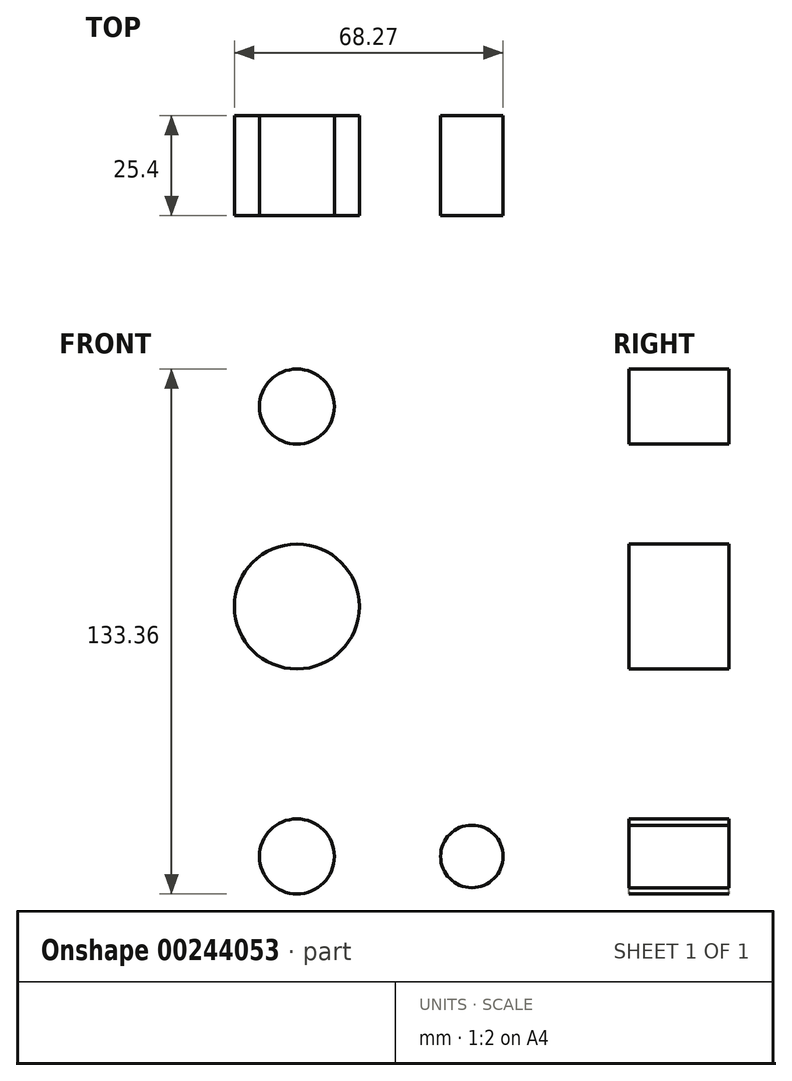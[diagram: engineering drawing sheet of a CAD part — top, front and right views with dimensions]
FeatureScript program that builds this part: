
annotation { "Feature Type Name" : "Feature", "Feature Type Description" : "" }
export const myFeature = defineFeature(function(context is Context, id is Id, definition is map)
    precondition{}
    {
        {
            var Q0;
            Q0=qCreatedBy(makeId("Front.planeOp"),FACE);
            var sketch = newSketch(context, id + "F0", { "sketchPlane" : qUnion([Q0])});
            skCircle(sketch, "E0", {"center": v(0, 0) * mm, "radius": 15.88 * mm});
            skCircle(sketch, "E1", {"center": v(0, 50.8) * mm, "radius": 9.53 * mm});
            skCircle(sketch, "E2", {"center": v(0, -63.5) * mm, "radius": 9.53 * mm});
            skCircle(sketch, "E3", {"center": v(44.45, -63.5) * mm, "radius": 7.94 * mm});
            skSolve(sketch);
        }
        {
            var Q0;
            Q0=qCreatedBy(makeId("Front.planeOp"),FACE);
            var sketch = newSketch(context, id + "F1", { "sketchPlane" : qUnion([Q0])});
            skLineSegment(sketch, "E4", {"start": v(9.46, 51.92) * mm, "end": v(16, 0) * mm});
            skLineSegment(sketch, "E5", {"start": v(16, 0) * mm, "end": v(10.25, -45.67) * mm});
            skLineSegment(sketch, "E6", {"start": v(-9.38, 52.57) * mm, "end": v(-16, 0) * mm});
            skLineSegment(sketch, "E7", {"start": v(-16, 0) * mm, "end": v(-8.14, -62.35) * mm});
            skLineSegment(sketch, "E8", {"start": v(17.85, -54.6) * mm, "end": v(45, -55.58) * mm});
            skLineSegment(sketch, "E9", {"start": v(0, -73.03) * mm, "end": v(45.77, -71.4) * mm});
            skPoint(sketch, "E10.newPointB", {"position": v(0, -53.97) * mm});
            skArc(sketch, "E10.filletArc", {"start": v(10.25, -45.67) * mm, "mid": v(12.08, -51.81) * mm, "end": v(17.85, -54.6) * mm});
            skSolve(sketch);
        }
        {
            var Q0;
            Q0 = qSketchRegion(id + "F0", true);
            var Q1;
            Q1 = qSketchRegion(id + "F1", true);
            extrude(context, id + "F2", {"entities" : qUnion([Q0, Q1]), "depth" : 25.4 * mm});
        }
        {
            var Q0;
            Q0=qCreatedBy(makeId("Front.planeOp"),FACE);
            var sketch = newSketch(context, id + "F3", { "sketchPlane" : qUnion([Q0])});
            skLineSegment(sketch, "E11.bottom", {"start": v(-30.12, 63.07) * mm, "end": v(57.42, 63.07) * mm});
            skLineSegment(sketch, "E11.top", {"start": v(-30.12, -74.6) * mm, "end": v(57.42, -74.6) * mm});
            skLineSegment(sketch, "E11.left", {"start": v(-30.12, 63.07) * mm, "end": v(-30.12, -74.6) * mm});
            skLineSegment(sketch, "E11.right", {"start": v(57.42, 63.07) * mm, "end": v(57.42, -74.6) * mm});
            skSolve(sketch);
        }
        {
            var Q0;
            Q0=makeQuery(id+"F3.imprint","IMPRINT",FACE,{"disambiguationData":[TD([[makeQuery(id+"F3.imprint","IMPRINT",EDGE,{"derivedFrom":sQuery(id+"F3.wireOp",EDGE,"E11.bottom")}),-1.0]])]});
            extrude(context, id + "F4", {"entities" : qUnion([Q0]), "operationType" : NewBodyOperationType.REMOVE, "oppositeDirection" : true, "depth" : 25.4 * mm});
        }
    });
